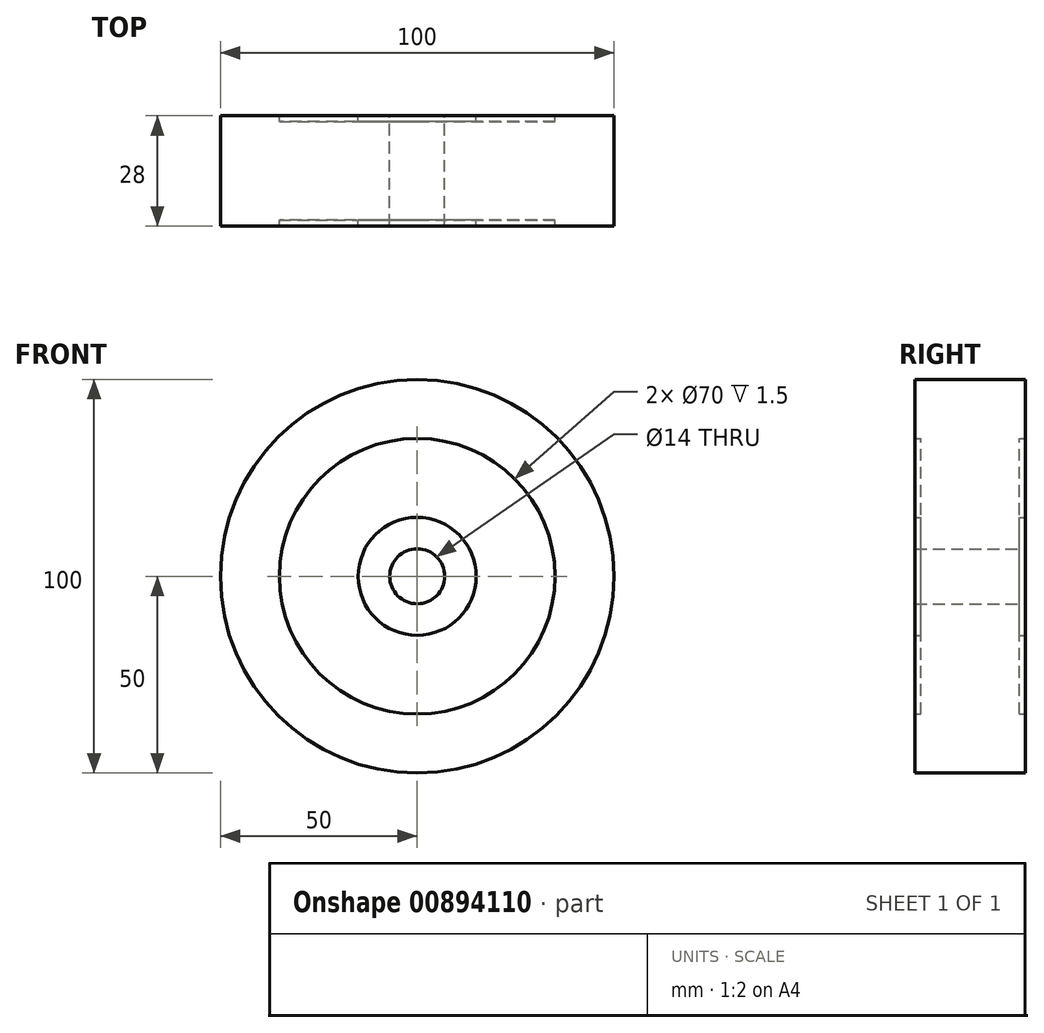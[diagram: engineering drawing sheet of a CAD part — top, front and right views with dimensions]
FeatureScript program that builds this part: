
annotation { "Feature Type Name" : "Feature", "Feature Type Description" : "" }
export const myFeature = defineFeature(function(context is Context, id is Id, definition is map)
    precondition{}
    {
        {
            var Q0;
            Q0=qCreatedBy(makeId("Front.planeOp"),FACE);
            var sketch = newSketch(context, id + "F0", { "sketchPlane" : qUnion([Q0])});
            skCircle(sketch, "E0", {"center": v(0, 0) * mm, "radius": 7 * mm});
            skCircle(sketch, "E1", {"center": v(0, 0) * mm, "radius": 15 * mm});
            skCircle(sketch, "E2", {"center": v(0, 0) * mm, "radius": 35 * mm});
            skCircle(sketch, "E3", {"center": v(0, 0) * mm, "radius": 50 * mm});
            skSolve(sketch);
        }
        {
            var Q0;
            Q0=makeQuery(id+"F0.imprint","IMPRINT",FACE,{"disambiguationData":[TD([[makeQuery(id+"F0.imprint","IMPRINT",EDGE,{"derivedFrom":sQuery(id+"F0.wireOp",EDGE,"E0")}),-1.0]])]});
            var Q1;
            Q1=makeQuery(id+"F0.imprint","IMPRINT",FACE,{"disambiguationData":[TD([[makeQuery(id+"F0.imprint","IMPRINT",EDGE,{"derivedFrom":sQuery(id+"F0.wireOp",EDGE,"E2")}),-1.0]])]});
            extrude(context, id + "F1", {"entities" : qUnion([Q0, Q1]), "endBound" : BoundingType.SYMMETRIC, "depth" : 28 * mm, "offsetDistance" : 25 * mm});
        }
        {
            var Q0;
            Q0 = qSketchRegion(id + "F0", true);
            var Q1;
            Q1=makeQuery(id+"F0.imprint","IMPRINT",FACE,{"disambiguationData":[TD([[makeQuery(id+"F0.imprint","IMPRINT",EDGE,{"derivedFrom":sQuery(id+"F0.wireOp",EDGE,"E1")}),-1.0]])]});
            extrude(context, id + "F2", {"entities" : qUnion([Q0, Q1]), "operationType" : NewBodyOperationType.ADD, "endBound" : BoundingType.SYMMETRIC, "depth" : 25 * mm, "offsetDistance" : 25 * mm});
        }
    });
